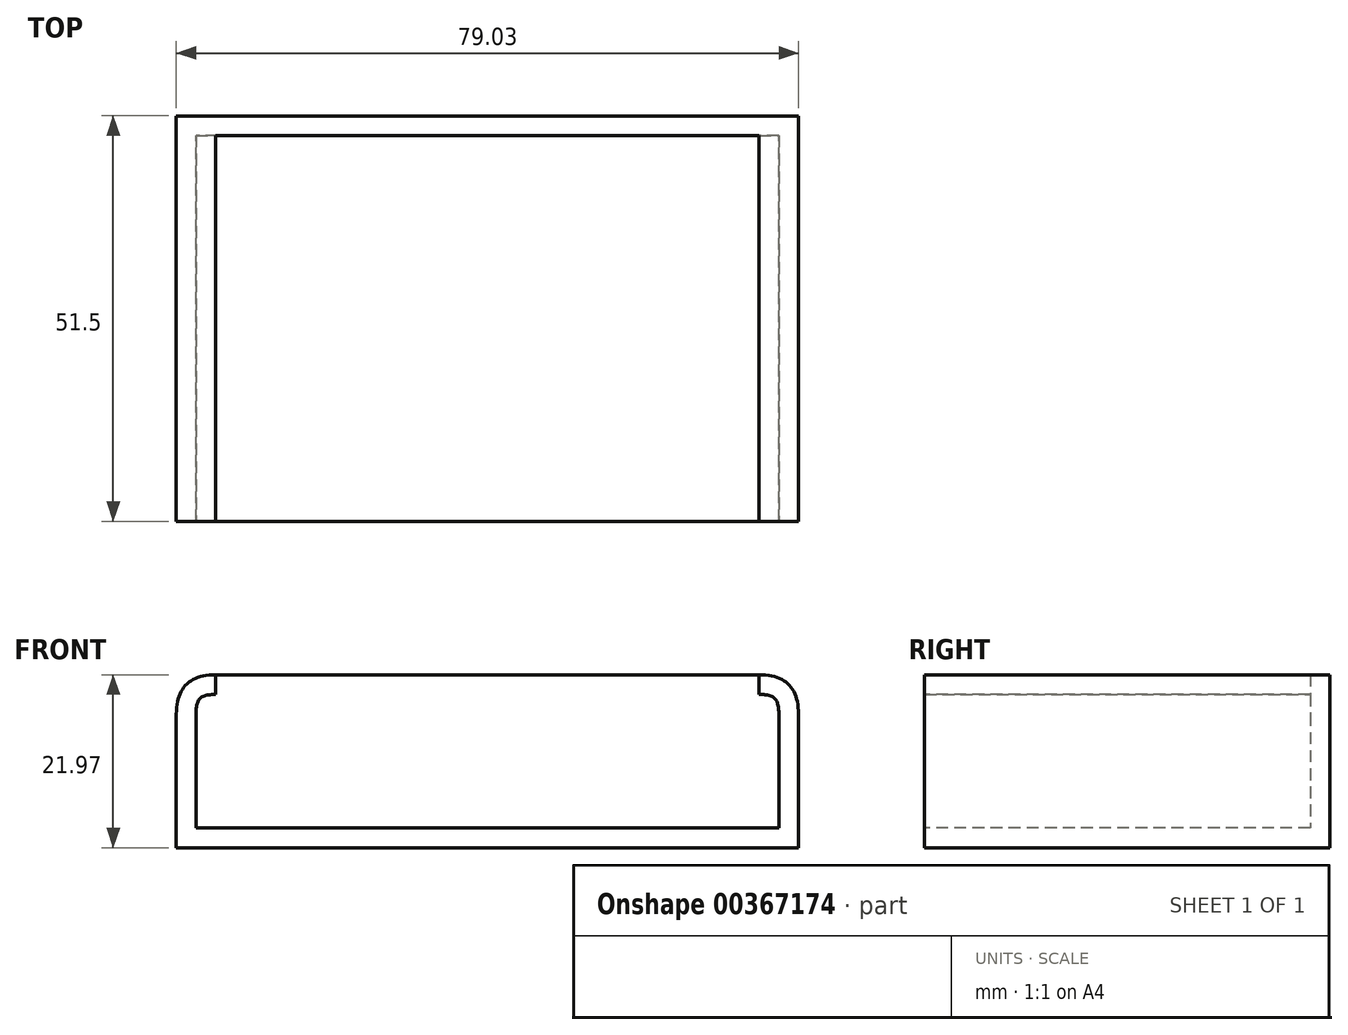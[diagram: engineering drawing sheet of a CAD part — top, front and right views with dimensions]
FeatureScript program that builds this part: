
annotation { "Feature Type Name" : "Feature", "Feature Type Description" : "" }
export const myFeature = defineFeature(function(context is Context, id is Id, definition is map)
    precondition{}
    {
        {
            var Q0;
            Q0=qCreatedBy(makeId("Top.planeOp"),FACE);
            var sketch = newSketch(context, id + "F0", { "sketchPlane" : qUnion([Q0])});
            skLineSegment(sketch, "E0", {"start": v(-43.8, -11.75) * mm, "end": v(35.24, -11.75) * mm});
            skLineSegment(sketch, "E1", {"start": v(35.24, -11.75) * mm, "end": v(35.24, 39.75) * mm});
            skLineSegment(sketch, "E2", {"start": v(35.24, 39.75) * mm, "end": v(-43.8, 39.75) * mm});
            skLineSegment(sketch, "E3", {"start": v(-43.8, 39.75) * mm, "end": v(-43.8, -11.75) * mm});
            skSolve(sketch);
        }
        {
            var Q0;
            Q0 = qSketchRegion(id + "F0", true);
            extrude(context, id + "F1", {"entities" : qUnion([Q0]), "depth" : 21.97 * mm});
        }
        {
            var Q0;
            Q0=makeQuery(id+"F1.opExtrude","CAP_EDGE",EDGE,{"disambiguationData":[OSD([sQuery(id+"F0.wireOp",EDGE,"E3")])],"isStart":false});
            var Q1;
            Q1=makeQuery(id+"F1.opExtrude","CAP_EDGE",EDGE,{"disambiguationData":[OSD([sQuery(id+"F0.wireOp",EDGE,"E1")])],"isStart":false});
            fillet(context, id + "F2", {"entities" : qUnion([Q0, Q1]), "radius" : 5 * mm, "tangentPropagation" : true, "rho" : 0.5, "crossSection" : FilletCrossSection.CONIC, "allowEdgeOverflow" : false});
        }
        {
            var Q0;
            Q0=makeQuery(id+"F1.opExtrude","CAP_FACE",FACE,{"disambiguationData":[OSD([sQuery(id+"F0.wireOp",EDGE,"E0"),sQuery(id+"F0.wireOp",EDGE,"E1"),sQuery(id+"F0.wireOp",EDGE,"E2"),sQuery(id+"F0.wireOp",EDGE,"E3")])],"isStart":false});
            var Q1;
            Q1=makeQuery(id+"F1.opExtrude","SWEPT_FACE",FACE,{"disambiguationData":[OSD([sQuery(id+"F0.wireOp",EDGE,"E0")])]});
            shell(context, id + "F3", {"entities" : qUnion([Q0, Q1]), "thickness" : 2.5 * mm});
        }
    });
